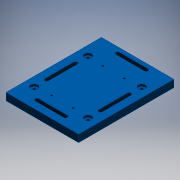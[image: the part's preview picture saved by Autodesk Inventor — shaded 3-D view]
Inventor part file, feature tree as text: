
AUTODESK INVENTOR PART (.ipt)
format: ipt  version: 2016 (Build 200138000, 138)  size: 204,800 bytes
history: native  units: mm
features: sketch x4, extrude x2, hole x2
ambient origin geometry x8: Origin, YZ Plane, XZ Plane, XY Plane, X Axis, Y Axis, Z Axis, Center Point
bodies: Solid1 (feature_tree)
feature tree (8):
  extrude  "flash4base"  Depth=10.0mm
  hole  "flash4mountingholes"  [1 undecoded]
  hole  "mountinPostMountingHoles"  [1 undecoded]
  extrude  "m6Alignment"  Depth=143.4mm
  sketch  "Sketch2"  dims[d9=120.0mm d10=125.0mm d11=7.0mm d12=4.0mm d13=10.0mm d16=125.0mm]
  sketch  "Sketch3"  dims[d17=62.5mm d18=85.0mm]
  sketch  "Sketch4"  dims[d19=42.5mm d20=25.0mm]
  sketch  "Sketch5"  dims[d21=25.0mm d23=22.5mm d24=13.5mm d25=0.0mm d26=40.0mm d27=20.0mm d28=95.3mm d29=47.65mm d30=3.4mm d31=6.0mm d32=11.0mm d33=2.6mm d34=14.3117mm d35=8.0mm d36=20.594885mm d37=100.0mm d38=50.0mm d39=100.0mm d40=4.5mm d41=6.0mm d42=13.0mm d43=3.4mm d44=14.3117mm d45=8.0mm d46=20.594885mm d48=6.6mm d50=6.6mm d52=30.0mm d53=30.0mm d54=30.0mm d55=30.0mm d56=50.0mm d57=2.0mm d58=3.0mm d59=3.0mm d60=10.0mm d61=0.0mm d62=6.6mm d63=6.6mm d64=30.0mm d65=30.0mm d66=30.0mm d67=30.0mm d70=3.0mm d71=93.4mm d72=46.7mm d73=143.4mm d74=65.0mm d75=30.0mm]
note: 2 required parameter values undecoded (feature->parameter linkage not recoverable at this tier; creation-order binding heuristic only, values carry confidence <= 0.55)
